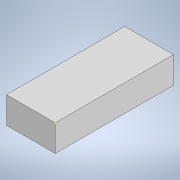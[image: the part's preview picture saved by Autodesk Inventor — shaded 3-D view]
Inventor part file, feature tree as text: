
AUTODESK INVENTOR PART (.ipt)
format: ipt  version: 2022 (Build 260153000, 153)  size: 93,696 bytes
history: native  units: mm
features: sketch x2, extrude x1
ambient origin geometry x8: Origin, YZ Plane, XZ Plane, XY Plane, X Axis, Y Axis, Z Axis, Center Point
bodies: Solid1 (feature_tree)
feature tree (3):
  extrude  "Extrusion1"  Depth=40.0mm
  sketch  "Sketch2"  dims[d2=9.0mm d3=0.0mm]
  sketch  "Sketch1"  dims[d0=16.5mm d1=40.0mm]
